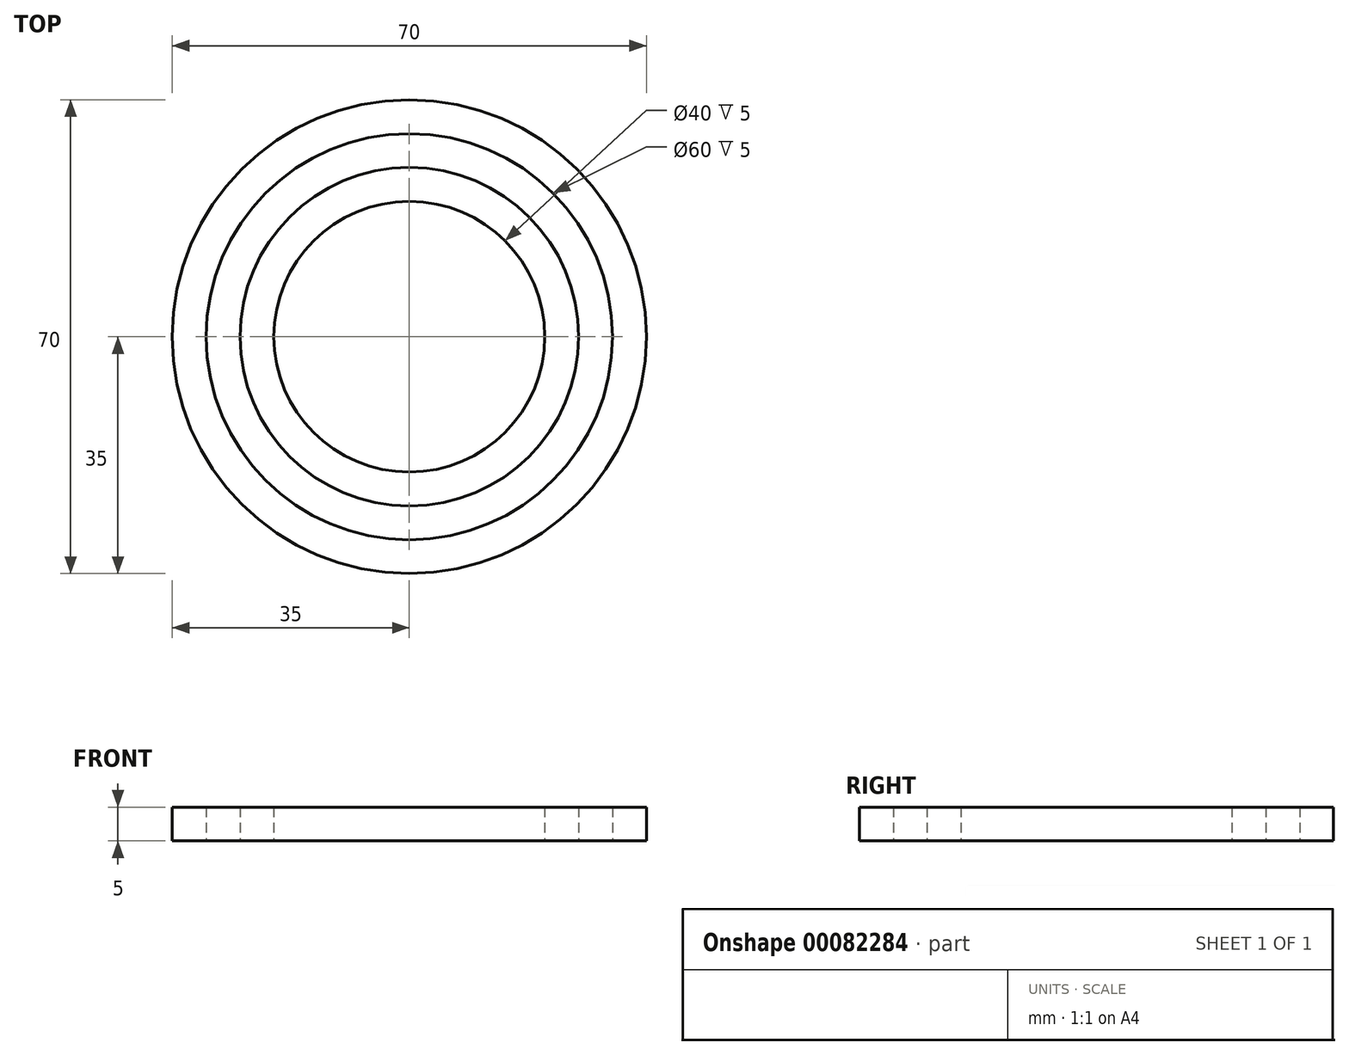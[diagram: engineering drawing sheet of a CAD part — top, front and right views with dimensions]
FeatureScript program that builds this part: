
annotation { "Feature Type Name" : "Feature", "Feature Type Description" : "" }
export const myFeature = defineFeature(function(context is Context, id is Id, definition is map)
    precondition{}
    {
        {
            var Q0;
            Q0=qCreatedBy(makeId("Top.planeOp"),FACE);
            var sketch = newSketch(context, id + "F0", { "sketchPlane" : qUnion([Q0])});
            skCircle(sketch, "E0", {"center": v(0, 0) * mm, "radius": 20 * mm});
            skCircle(sketch, "E1", {"center": v(0, 0) * mm, "radius": 25 * mm});
            skCircle(sketch, "E2", {"center": v(0, 0) * mm, "radius": 30 * mm});
            skCircle(sketch, "E3", {"center": v(0, 0) * mm, "radius": 35 * mm});
            skSolve(sketch);
        }
        {
            var Q0;
            Q0=makeQuery(id+"F0.imprint","IMPRINT",FACE,{"disambiguationData":[TD([[makeQuery(id+"F0.imprint","IMPRINT",EDGE,{"derivedFrom":sQuery(id+"F0.wireOp",EDGE,"E0")}),-1.0]])]});
            var Q1;
            Q1=makeQuery(id+"F0.imprint","IMPRINT",FACE,{"disambiguationData":[TD([[makeQuery(id+"F0.imprint","IMPRINT",EDGE,{"derivedFrom":sQuery(id+"F0.wireOp",EDGE,"E2")}),-1.0]])]});
            extrude(context, id + "F1", {"entities" : qUnion([Q0, Q1]), "depth" : 5 * mm, "offsetDistance" : 25 * mm});
        }
    });
